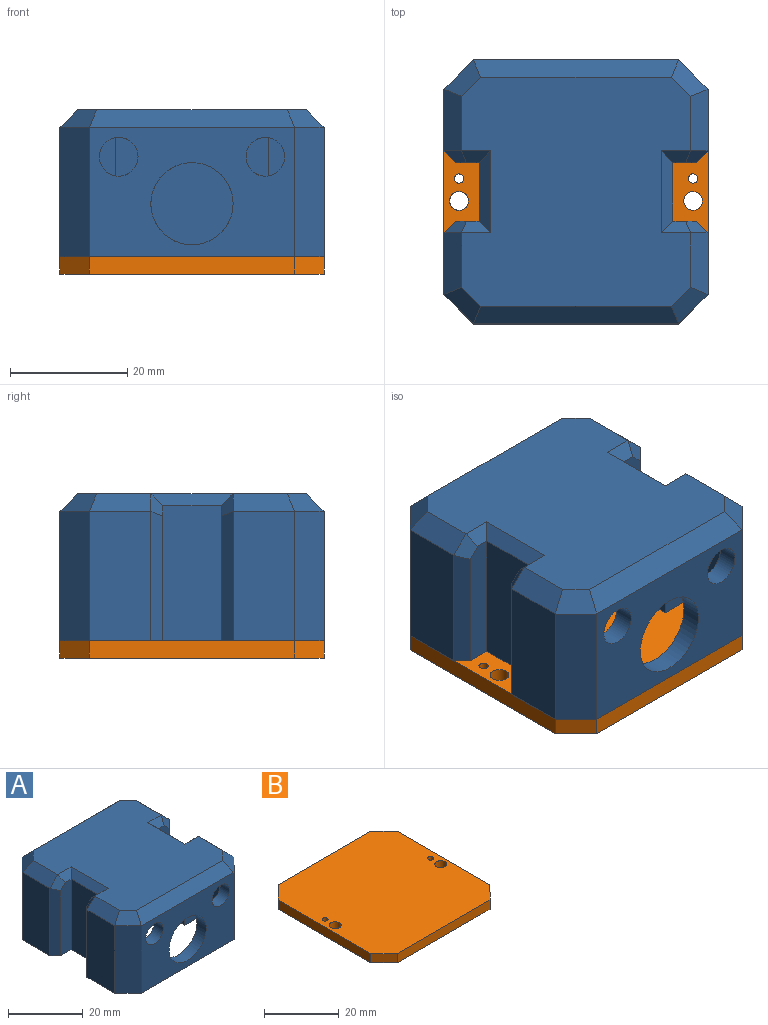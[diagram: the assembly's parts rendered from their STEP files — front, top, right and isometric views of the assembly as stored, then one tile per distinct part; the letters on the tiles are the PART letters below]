
ASSEMBLY  parts=2 mates=1
PART A: 114 faces, bbox 45x45x25 mm
  f0: plane 40x40mm, normal (0,0,-1), area 171.8mm2, adj f44,f45,f48,f49,f50,f51,f52,f53
  f1: plane 45x45mm, normal (0,0,-1), area 185mm2, adj f2,f3,f7,f8,f9,f10,f11,f12
  f2: plane 22x10.5mm, normal (-1,0,0), area 231mm2, adj f1,f14,f15,f41
  f3: plane 22x10.5mm, normal (1,0,0), area 231mm2, adj f1,f6,f12,f40
  f4: plane 39x39mm, normal (0,0,1), area 1360mm2, adj f5,f6,f15,f16,f17,f18,f19,f20
  f5: plane 10.5x3mm, normal (-0.71,0,0.71), area 41.9mm2, adj f4,f7,f16,f34
  f6: plane 10.5x3mm, normal (0.71,0,0.71), area 41.9mm2, adj f3,f4,f21,f29
  f7: plane 22x10.5mm, normal (-1,0,0), area 231mm2, adj f1,f5,f13,f42
  f8: plane 35x22mm, normal (0,-1,0), area 547.6mm2, adj f1,f12,f14,f19,f70,f71,f72
  f9: plane 22x10.5mm, normal (1,0,0), area 231mm2, adj f1,f11,f22,f39
  f10: plane 35x22mm, normal (0,1,0), area 770mm2, adj f1,f11,f13,f18
  f11: plane 22x5mm, normal (0.71,0.71,0), area 155.6mm2, adj f1,f9,f10,f20
  f12: plane 22x5mm, normal (0.71,-0.71,0), area 155.6mm2, adj f1,f3,f8,f21
  f13: plane 22x5mm, normal (-0.71,0.71,0), area 155.6mm2, adj f1,f7,f10,f16
  f14: plane 22x5mm, normal (-0.71,-0.71,0), area 155.6mm2, adj f1,f2,f8,f17
  f15: plane 10.5x3mm, normal (-0.71,0,0.71), area 41.9mm2, adj f2,f4,f17,f38
  f16: plane 6.24x6.24mm, normal (-0.5,0.5,0.71), area 24.7mm2, adj f4,f5,f13,f18
  f17: plane 6.24x6.24mm, normal (-0.5,-0.5,0.71), area 24.7mm2, adj f4,f14,f15,f19
  f18: plane 35x3mm, normal (0,0.71,0.71), area 143.2mm2, adj f4,f10,f16,f20
  f19: plane 35x3mm, normal (0,-0.71,0.71), area 143.2mm2, adj f4,f8,f17,f21
  f20: plane 6.24x6.24mm, normal (0.5,0.5,0.71), area 24.7mm2, adj f4,f11,f18,f22
  f21: plane 6.24x6.24mm, normal (0.5,-0.5,0.71), area 24.7mm2, adj f4,f6,f12,f19
  f22: plane 10.5x3mm, normal (0.71,0,0.71), area 41.9mm2, adj f4,f9,f20,f33
  f23: plane 23x10mm, normal (1,0,0), area 230mm2, adj f1,f24,f25,f31
  f24: plane 23x4mm, normal (0,-1,0), area 90.3mm2, adj f1,f23,f32,f33,f39
  f25: plane 23x4mm, normal (0,1,0), area 90.3mm2, adj f1,f23,f29,f30,f40
  f26: plane 23x10mm, normal (-1,0,0), area 230mm2, adj f1,f27,f28,f36
  f27: plane 23x4mm, normal (0,-1,0), area 90.3mm2, adj f1,f26,f34,f35,f42
  f28: plane 23x4mm, normal (0,1,0), area 90.3mm2, adj f1,f26,f37,f38,f41
  f29: plane 3.83x3.83mm, normal (0.5,0.71,0.5), area 9.7mm2, adj f6,f25,f30,f40
  f30: plane 5x2mm, normal (0,0.71,0.71), area 10.1mm2, adj f4,f25,f29,f31
  f31: plane 14x2mm, normal (0.71,0,0.71), area 33.9mm2, adj f4,f23,f30,f32
  f32: plane 5x2mm, normal (0,-0.71,0.71), area 10.1mm2, adj f4,f24,f31,f33
  f33: plane 3.83x3.83mm, normal (0.5,-0.71,0.5), area 9.7mm2, adj f22,f24,f32,f39
  f34: plane 3.83x3.83mm, normal (-0.5,-0.71,0.5), area 9.7mm2, adj f5,f27,f35,f42
  f35: plane 5x2mm, normal (0,-0.71,0.71), area 10.1mm2, adj f4,f27,f34,f36
  f36: plane 14x2mm, normal (-0.71,0,0.71), area 33.9mm2, adj f4,f26,f35,f37
  f37: plane 5x2mm, normal (0,0.71,0.71), area 10.1mm2, adj f4,f28,f36,f38
  f38: plane 3.83x3.83mm, normal (-0.5,0.71,0.5), area 9.7mm2, adj f15,f28,f37,f41
  f39: plane 22x2mm, normal (0.71,-0.71,0), area 61.1mm2, adj f1,f9,f24,f33
  f40: plane 22x2mm, normal (0.71,0.71,0), area 61.1mm2, adj f1,f3,f25,f29
  f41: plane 22x2mm, normal (-0.71,0.71,0), area 61.1mm2, adj f1,f2,f28,f38
  f42: plane 22x2mm, normal (-0.71,-0.71,0), area 61.1mm2, adj f1,f7,f27,f34
  f43: plane 36.1x36.1mm, normal (0,0,-1), area 1120.1mm2, adj f46,f47,f56,f57,f58,f59,f60,f61
  f44: plane 20.55x7.55mm, normal (1,0,0), area 155.2mm2, adj f0,f55,f56,f69
  f45: plane 20.55x7.55mm, normal (-1,0,0), area 155.2mm2, adj f0,f47,f53,f66
  f46: plane 7.55x0.95mm, normal (0.71,0,-0.71), area 9.9mm2, adj f43,f48,f57,f68
  f47: plane 7.55x0.95mm, normal (-0.71,0,-0.71), area 9.9mm2, adj f43,f45,f62,f66
  f48: plane 20.55x7.55mm, normal (1,0,0), area 155.2mm2, adj f0,f46,f54,f68
  f49: plane 32.1x20.55mm, normal (0,1,0), area 437.3mm2, adj f0,f53,f55,f60,f70,f71,f72
  f50: plane 20.55x7.55mm, normal (-1,0,0), area 155.2mm2, adj f0,f52,f63,f65
  f51: plane 32.1x20.55mm, normal (0,-1,0), area 659.7mm2, adj f0,f52,f54,f59
  f52: plane 20.55x2.95mm, normal (-0.71,-0.71,0), area 85.7mm2, adj f0,f50,f51,f61
  f53: plane 20.55x2.95mm, normal (-0.71,0.71,0), area 85.7mm2, adj f0,f45,f49,f62
  f54: plane 20.55x2.95mm, normal (0.71,-0.71,0), area 85.7mm2, adj f0,f48,f51,f57
  f55: plane 20.55x2.95mm, normal (0.71,0.71,0), area 85.7mm2, adj f0,f44,f49,f58
  f56: plane 7.55x0.95mm, normal (0.71,0,-0.71), area 9.9mm2, adj f43,f44,f58,f69
  f57: plane 3.34x3.34mm, normal (0.5,-0.5,-0.71), area 5.1mm2, adj f43,f46,f54,f59
  f58: plane 3.34x3.34mm, normal (0.5,0.5,-0.71), area 5.1mm2, adj f43,f55,f56,f60
  f59: plane 32.1x0.95mm, normal (0,-0.71,-0.71), area 42.6mm2, adj f43,f51,f57,f61
  f60: plane 32.1x0.95mm, normal (0,0.71,-0.71), area 42.6mm2, adj f43,f49,f58,f62
  f61: plane 3.34x3.34mm, normal (-0.5,-0.5,-0.71), area 5.1mm2, adj f43,f52,f59,f63
  f62: plane 3.34x3.34mm, normal (-0.5,0.5,-0.71), area 5.1mm2, adj f43,f47,f53,f60
  f63: plane 7.55x0.95mm, normal (-0.71,0,-0.71), area 9.9mm2, adj f43,f50,f61,f65
  f64: plane 21.5x17mm, normal (-1,0,0), area 365.5mm2, adj f0,f43,f65,f66
  f65: plane 21.5x6mm, normal (0,1,0), area 128.5mm2, adj f0,f43,f50,f63,f64
  f66: plane 21.5x6mm, normal (0,-1,0), area 128.5mm2, adj f0,f43,f45,f47,f64
  f67: plane 21.5x17mm, normal (1,0,0), area 365.5mm2, adj f0,f43,f68,f69
  f68: plane 21.5x6mm, normal (0,1,0), area 128.5mm2, adj f0,f43,f46,f48,f67
  f69: plane 21.5x6mm, normal (0,-1,0), area 128.5mm2, adj f0,f43,f44,f56,f67
  f70: cylinder r=7mm len=14mm, axis (0,-1,0), area 153.9mm2, adj f8,f49
  f71: cylinder r=3.3mm len=6.6mm, axis (0,-1,0), area 72.6mm2, adj f8,f49
  f72: cylinder r=3.3mm len=6.6mm, axis (0,-1,0), area 72.6mm2, adj f8,f49
  f73: plane 34.17x1.2mm, normal (0,-1,0), area 41mm2, adj f1,f74,f112,f113
  f74: plane 4.41x4.41mm, normal (-0.71,-0.71,0), area 7.5mm2, adj f1,f73,f75,f113
  f75: plane 9.67x1.2mm, normal (-1,0,0), area 11.6mm2, adj f1,f74,f76,f113
  f76: plane 1.41x1.41mm, normal (-0.71,0.71,0), area 2.4mm2, adj f1,f75,f77,f113
  f77: plane 4.59x1.2mm, normal (0,1,0), area 5.5mm2, adj f1,f76,f78,f113
  f78: plane 12x1.2mm, normal (-1,0,0), area 14.4mm2, adj f1,f77,f79,f113
  f79: plane 4.59x1.2mm, normal (0,-1,0), area 5.5mm2, adj f1,f78,f80,f113
  f80: plane 1.41x1.41mm, normal (-0.71,-0.71,0), area 2.4mm2, adj f1,f79,f81,f113
  f81: plane 9.67x1.2mm, normal (-1,0,0), area 11.6mm2, adj f1,f80,f82,f113
  f82: plane 4.41x4.41mm, normal (-0.71,0.71,0), area 7.5mm2, adj f1,f81,f83,f113
  f83: plane 34.17x1.2mm, normal (0,1,0), area 41mm2, adj f1,f82,f84,f113
  f84: plane 4.41x4.41mm, normal (0.71,0.71,0), area 7.5mm2, adj f1,f83,f85,f113
  f85: plane 9.67x1.2mm, normal (1,0,0), area 11.6mm2, adj f1,f84,f86,f113
  f86: plane 1.41x1.41mm, normal (0.71,-0.71,0), area 2.4mm2, adj f1,f85,f87,f113
  f87: plane 4.59x1.2mm, normal (0,-1,0), area 5.5mm2, adj f1,f86,f88,f113
  f88: plane 12x1.2mm, normal (1,0,0), area 14.4mm2, adj f1,f87,f89,f113
  f89: plane 4.59x1.2mm, normal (0,1,0), area 5.5mm2, adj f1,f88,f90,f113
  f90: plane 1.41x1.41mm, normal (0.71,0.71,0), area 2.4mm2, adj f1,f89,f91,f113
  f91: plane 9.67x1.2mm, normal (1,0,0), area 11.6mm2, adj f1,f90,f112,f113
  f92: plane 15x1.2mm, normal (1,0,0), area 18mm2, adj f0,f93,f111,f113
  f93: plane 5.46x1.2mm, normal (0,-1,0), area 6.6mm2, adj f0,f92,f94,f113
  f94: plane 1.2x0.54mm, normal (0.71,-0.71,0), area 0.9mm2, adj f0,f93,f95,f113
  f95: plane 8.43x1.2mm, normal (1,0,0), area 10.1mm2, adj f0,f94,f96,f113
  f96: plane 3.54x3.54mm, normal (0.71,0.71,0), area 6mm2, adj f0,f95,f97,f113
  f97: plane 32.93x1.2mm, normal (0,1,0), area 39.5mm2, adj f0,f96,f98,f113
  f98: plane 3.54x3.54mm, normal (-0.71,0.71,0), area 6mm2, adj f0,f97,f99,f113
  f99: plane 8.43x1.2mm, normal (-1,0,0), area 10.1mm2, adj f0,f98,f100,f113
  f100: plane 1.2x0.54mm, normal (-0.71,-0.71,0), area 0.9mm2, adj f0,f99,f101,f113
  f101: plane 5.46x1.2mm, normal (0,-1,0), area 6.6mm2, adj f0,f100,f102,f113
  f102: plane 15x1.2mm, normal (-1,0,0), area 18mm2, adj f0,f101,f103,f113
  f103: plane 5.46x1.2mm, normal (0,1,0), area 6.6mm2, adj f0,f102,f104,f113
  f104: plane 1.2x0.54mm, normal (-0.71,0.71,0), area 0.9mm2, adj f0,f103,f105,f113
  f105: plane 8.43x1.2mm, normal (-1,0,0), area 10.1mm2, adj f0,f104,f106,f113
  f106: plane 3.54x3.54mm, normal (-0.71,-0.71,0), area 6mm2, adj f0,f105,f107,f113
  f107: plane 32.93x1.2mm, normal (0,-1,0), area 39.5mm2, adj f0,f106,f108,f113
  f108: plane 3.54x3.54mm, normal (0.71,-0.71,0), area 6mm2, adj f0,f107,f109,f113
  f109: plane 8.43x1.2mm, normal (1,0,0), area 10.1mm2, adj f0,f108,f110,f113
  f110: plane 1.2x0.54mm, normal (0.71,0.71,0), area 0.9mm2, adj f0,f109,f111,f113
  f111: plane 5.46x1.2mm, normal (0,1,0), area 6.6mm2, adj f0,f92,f110,f113
  f112: plane 4.41x4.41mm, normal (0.71,-0.71,0), area 7.5mm2, adj f1,f73,f91,f113
  f113: plane 43x43mm, normal (0,0,-1), area 267.6mm2, adj f73,f74,f75,f76,f77,f78,f79,f80
PART B: 14 faces, bbox 45x45x3 mm
  f0: plane 45x45mm, normal (0,0,1), area 1954.9mm2, adj f2,f3,f4,f5,f6,f7,f8,f9
  f1: plane 45x45mm, normal (0,0,-1), area 1954.9mm2, adj f2,f3,f4,f5,f6,f7,f8,f9
  f2: plane 5x5mm, normal (-0.71,-0.71,0), area 21.2mm2, adj f0,f1,f3,f9
  f3: plane 35x3mm, normal (0,-1,0), area 105mm2, adj f0,f1,f2,f4
  f4: plane 5x5mm, normal (0.71,-0.71,0), area 21.2mm2, adj f0,f1,f3,f5
  f5: plane 35x3mm, normal (1,0,0), area 105mm2, adj f0,f1,f4,f6
  f6: plane 5x5mm, normal (0.71,0.71,0), area 21.2mm2, adj f0,f1,f5,f7
  f7: plane 35x3mm, normal (0,1,0), area 105mm2, adj f0,f1,f6,f8
  f8: plane 5x5mm, normal (-0.71,0.71,0), area 21.2mm2, adj f0,f1,f7,f9
  f9: plane 35x3mm, normal (-1,0,0), area 105mm2, adj f0,f1,f2,f8
  f10: cylinder r=1.6mm len=3.2mm, axis (0,0,1), area 30.2mm2, adj f0,f1
  f11: cylinder r=0.8mm len=3mm, axis (0,0,1), area 15mm2, adj f0,f1
  f12: cylinder r=1.6mm len=3.2mm, axis (0,0,1), area 30.2mm2, adj f0,f1
  f13: cylinder r=0.8mm len=3mm, axis (0,0,1), area 15mm2, adj f0,f1
PLACE A t=(4.44,1.04,-7.96)mm
PLACE B t=(4.44,1.04,-10.96)mm fixed
MATE fastened B.f3 <-> A.f8  axis (0,-1,0) through (4.44,-21.46,-7.96)mm
